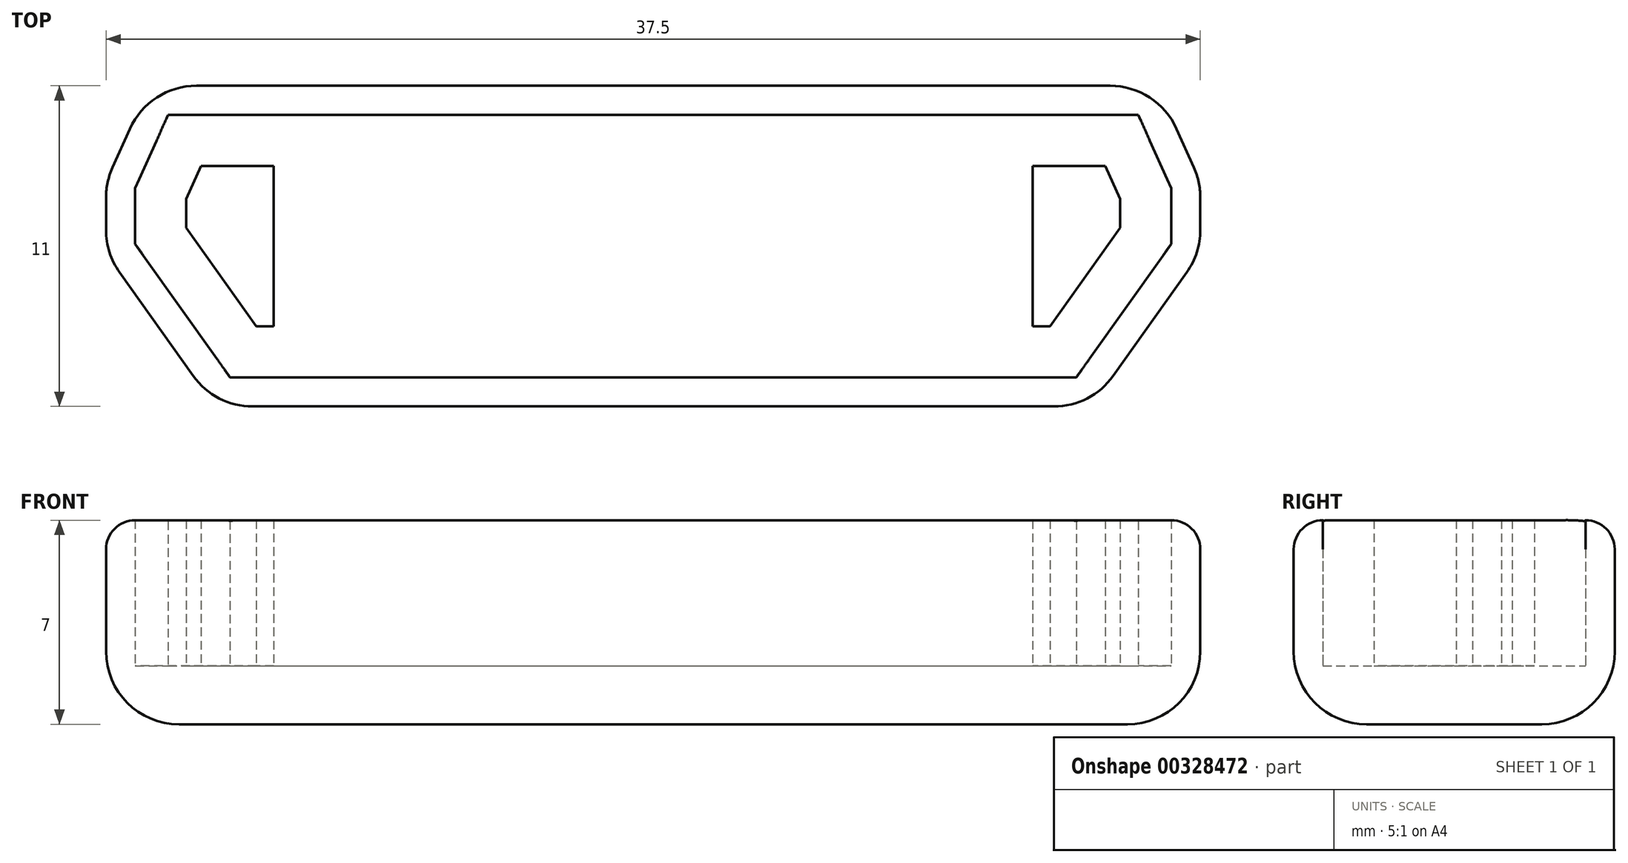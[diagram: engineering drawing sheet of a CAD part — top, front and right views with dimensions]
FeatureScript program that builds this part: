
annotation { "Feature Type Name" : "Feature", "Feature Type Description" : "" }
export const myFeature = defineFeature(function(context is Context, id is Id, definition is map)
    precondition{}
    {
        {
            var Q0;
            Q0=qCreatedBy(makeId("Top.planeOp"),FACE);
            var sketch = newSketch(context, id + "F0", { "sketchPlane" : qUnion([Q0])});
            skLineSegment(sketch, "E0", {"start": v(0, 0) * mm, "end": v(0, 26.86) * mm, "construction": true});
            skLineSegment(sketch, "E1", {"start": v(0, 0) * mm, "end": v(14.5, 0) * mm});
            skLineSegment(sketch, "E2", {"start": v(14.5, 0) * mm, "end": v(17.75, 4.57) * mm});
            skLineSegment(sketch, "E3", {"start": v(17.75, 4.57) * mm, "end": v(17.75, 6.5) * mm});
            skLineSegment(sketch, "E4", {"start": v(17.75, 6.5) * mm, "end": v(16.62, 9) * mm});
            skLineSegment(sketch, "E5", {"start": v(16.62, 9) * mm, "end": v(0, 9) * mm});
            skLineSegment(sketch, "E6.0", {"start": v(17.27, 10) * mm, "end": v(0, 10) * mm});
            skLineSegment(sketch, "E6.1", {"start": v(0, -1) * mm, "end": v(15.02, -1) * mm});
            skLineSegment(sketch, "E6.2", {"start": v(15.02, -1) * mm, "end": v(18.75, 4.25) * mm});
            skLineSegment(sketch, "E6.3", {"start": v(18.75, 4.25) * mm, "end": v(18.75, 6.7) * mm});
            skLineSegment(sketch, "E6.4", {"start": v(18.75, 6.7) * mm, "end": v(17.27, 10) * mm});
            skLineSegment(sketch, "E7.0", {"start": v(15.5, 7.25) * mm, "end": v(13, 7.25) * mm});
            skLineSegment(sketch, "E7.1", {"start": v(13, 1.75) * mm, "end": v(13.6, 1.75) * mm});
            skLineSegment(sketch, "E7.2", {"start": v(13.6, 1.75) * mm, "end": v(16, 5.13) * mm});
            skLineSegment(sketch, "E7.3", {"start": v(16, 5.13) * mm, "end": v(16, 6.12) * mm});
            skLineSegment(sketch, "E7.4", {"start": v(16, 6.12) * mm, "end": v(15.5, 7.25) * mm});
            skLineSegment(sketch, "E8", {"start": v(13, 7.25) * mm, "end": v(13, 1.75) * mm});
            skLineSegment(sketch, "E9.MirrorCS", {"start": v(-16, 6.12) * mm, "end": v(-15.5, 7.25) * mm});
            skLineSegment(sketch, "E10.MirrorCS", {"start": v(-16, 5.13) * mm, "end": v(-16, 6.12) * mm});
            skLineSegment(sketch, "E11.MirrorCS", {"start": v(-13, 1.75) * mm, "end": v(-13.6, 1.75) * mm});
            skLineSegment(sketch, "E12.MirrorCS", {"start": v(-18.75, 4.25) * mm, "end": v(-18.75, 6.7) * mm});
            skLineSegment(sketch, "E13.MirrorCS", {"start": v(-17.75, 4.57) * mm, "end": v(-17.75, 6.5) * mm});
            skLineSegment(sketch, "E14.MirrorCS", {"start": v(-13, 7.25) * mm, "end": v(-13, 1.75) * mm});
            skLineSegment(sketch, "E15.MirrorCS", {"start": v(-13.6, 1.75) * mm, "end": v(-16, 5.13) * mm});
            skLineSegment(sketch, "E16.MirrorCS", {"start": v(-15.5, 7.25) * mm, "end": v(-13, 7.25) * mm});
            skLineSegment(sketch, "E17.MirrorCS", {"start": v(-18.75, 6.7) * mm, "end": v(-17.27, 10) * mm});
            skLineSegment(sketch, "E18.MirrorCS", {"start": v(-15.02, -1) * mm, "end": v(-18.75, 4.25) * mm});
            skLineSegment(sketch, "E19.MirrorCS", {"start": v(0, -1) * mm, "end": v(-15.02, -1) * mm});
            skLineSegment(sketch, "E20.MirrorCS", {"start": v(-17.27, 10) * mm, "end": v(0, 10) * mm});
            skLineSegment(sketch, "E21.MirrorCS", {"start": v(-16.62, 9) * mm, "end": v(0, 9) * mm});
            skLineSegment(sketch, "E22.MirrorCS", {"start": v(0, 0) * mm, "end": v(-14.5, 0) * mm});
            skLineSegment(sketch, "E23.MirrorCS", {"start": v(-17.75, 6.5) * mm, "end": v(-16.62, 9) * mm});
            skLineSegment(sketch, "E24.MirrorCS", {"start": v(-14.5, 0) * mm, "end": v(-17.75, 4.57) * mm});
            skSolve(sketch);
        }
        {
            var Q0;
            Q0=makeQuery(id+"F0.imprint","IMPRINT",FACE,{"disambiguationData":[TD([[makeQuery(id+"F0.imprint","IMPRINT",EDGE,{"derivedFrom":sQuery(id+"F0.wireOp",EDGE,"E1")}),-1.0]])]});
            var Q1;
            Q1=makeQuery(id+"F0.imprint","IMPRINT",FACE,{"disambiguationData":[TD([[makeQuery(id+"F0.imprint","IMPRINT",EDGE,{"derivedFrom":sQuery(id+"F0.wireOp",EDGE,"E9.MirrorCS")}),-1.0]])]});
            var Q2;
            Q2=makeQuery(id+"F0.imprint","IMPRINT",FACE,{"disambiguationData":[TD([[makeQuery(id+"F0.imprint","IMPRINT",EDGE,{"derivedFrom":sQuery(id+"F0.wireOp",EDGE,"E7.0")}),1.0]])]});
            extrude(context, id + "F1", {"entities" : qUnion([Q0, Q1, Q2]), "depth" : 5 * mm});
        }
        {
            var Q0;
            Q0=makeQuery(id+"F1.opExtrude","CAP_FACE",FACE,{"disambiguationData":[OSD([sQuery(id+"F0.wireOp",EDGE,"E1"),sQuery(id+"F0.wireOp",EDGE,"E2"),sQuery(id+"F0.wireOp",EDGE,"E3"),sQuery(id+"F0.wireOp",EDGE,"E4"),sQuery(id+"F0.wireOp",EDGE,"E5"),sQuery(id+"F0.wireOp",EDGE,"E6.0"),sQuery(id+"F0.wireOp",EDGE,"E6.1"),sQuery(id+"F0.wireOp",EDGE,"E6.2"),sQuery(id+"F0.wireOp",EDGE,"E6.3"),sQuery(id+"F0.wireOp",EDGE,"E6.4"),sQuery(id+"F0.wireOp",EDGE,"E12.MirrorCS"),sQuery(id+"F0.wireOp",EDGE,"E13.MirrorCS"),sQuery(id+"F0.wireOp",EDGE,"E17.MirrorCS"),sQuery(id+"F0.wireOp",EDGE,"E18.MirrorCS"),sQuery(id+"F0.wireOp",EDGE,"E19.MirrorCS"),sQuery(id+"F0.wireOp",EDGE,"E20.MirrorCS"),sQuery(id+"F0.wireOp",EDGE,"E21.MirrorCS"),sQuery(id+"F0.wireOp",EDGE,"E22.MirrorCS"),sQuery(id+"F0.wireOp",EDGE,"E23.MirrorCS"),sQuery(id+"F0.wireOp",EDGE,"E24.MirrorCS")])],"isStart":true});
            var sketch = newSketch(context, id + "F2", { "sketchPlane" : qUnion([Q0])});
            skLineSegment(sketch, "E25.0", {"start": v(17.27, -10) * mm, "end": v(-17.27, -10) * mm});
            skLineSegment(sketch, "E25.1", {"start": v(-18.75, -6.7) * mm, "end": v(-17.27, -10) * mm});
            skLineSegment(sketch, "E25.2", {"start": v(-18.75, -4.25) * mm, "end": v(-18.75, -6.7) * mm});
            skLineSegment(sketch, "E25.3", {"start": v(-15.02, 1) * mm, "end": v(-18.75, -4.25) * mm});
            skLineSegment(sketch, "E25.4", {"start": v(15.02, 1) * mm, "end": v(-15.02, 1) * mm});
            skLineSegment(sketch, "E25.5", {"start": v(15.02, 1) * mm, "end": v(18.75, -4.25) * mm});
            skLineSegment(sketch, "E25.6", {"start": v(18.75, -4.25) * mm, "end": v(18.75, -6.7) * mm});
            skLineSegment(sketch, "E25.7", {"start": v(18.75, -6.7) * mm, "end": v(17.27, -10) * mm});
            skSolve(sketch);
        }
        {
            var Q0;
            Q0 = qSketchRegion(id + "F2", true);
            extrude(context, id + "F3", {"entities" : qUnion([Q0]), "operationType" : NewBodyOperationType.ADD, "depth" : 2 * mm});
        }
        {
            var Q0;
            Q0=makeQuery(id+"F3.opExtrude","CAP_FACE",FACE,{"disambiguationData":[OSD([sQuery(id+"F2.wireOp",EDGE,"E25.0"),sQuery(id+"F2.wireOp",EDGE,"E25.1"),sQuery(id+"F2.wireOp",EDGE,"E25.2"),sQuery(id+"F2.wireOp",EDGE,"E25.3"),sQuery(id+"F2.wireOp",EDGE,"E25.4"),sQuery(id+"F2.wireOp",EDGE,"E25.5"),sQuery(id+"F2.wireOp",EDGE,"E25.6"),sQuery(id+"F2.wireOp",EDGE,"E25.7")])],"isStart":false});
            var Q1;
            Q1=makeQuery(id+"F3.boolean.opBoolean","MERGE",EDGE,{"derivedFrom":[makeQuery(id+"F1.opExtrude","SWEPT_EDGE",EDGE,{"disambiguationData":[OSD([sQuery(id+"F0.wireOp",EDGE,"E18.MirrorCS"),sQuery(id+"F0.wireOp",EDGE,"E19.MirrorCS")])]}),makeQuery(id+"F3.opExtrude","SWEPT_EDGE",EDGE,{"disambiguationData":[OSD([sQuery(id+"F2.wireOp",EDGE,"E25.3"),sQuery(id+"F2.wireOp",EDGE,"E25.4")])]})]});
            var Q2;
            Q2=makeQuery(id+"F3.boolean.opBoolean","MERGE",EDGE,{"derivedFrom":[makeQuery(id+"F1.opExtrude","SWEPT_EDGE",EDGE,{"disambiguationData":[OSD([sQuery(id+"F0.wireOp",EDGE,"E12.MirrorCS"),sQuery(id+"F0.wireOp",EDGE,"E18.MirrorCS")])]}),makeQuery(id+"F3.opExtrude","SWEPT_EDGE",EDGE,{"disambiguationData":[OSD([sQuery(id+"F2.wireOp",EDGE,"E25.2"),sQuery(id+"F2.wireOp",EDGE,"E25.3")])]})]});
            var Q3;
            Q3=makeQuery(id+"F3.boolean.opBoolean","MERGE",EDGE,{"derivedFrom":[makeQuery(id+"F1.opExtrude","SWEPT_EDGE",EDGE,{"disambiguationData":[OSD([sQuery(id+"F0.wireOp",EDGE,"E12.MirrorCS"),sQuery(id+"F0.wireOp",EDGE,"E17.MirrorCS")])]}),makeQuery(id+"F3.opExtrude","SWEPT_EDGE",EDGE,{"disambiguationData":[OSD([sQuery(id+"F2.wireOp",EDGE,"E25.1"),sQuery(id+"F2.wireOp",EDGE,"E25.2")])]})]});
            var Q4;
            Q4=makeQuery(id+"F3.boolean.opBoolean","MERGE",EDGE,{"derivedFrom":[makeQuery(id+"F1.opExtrude","SWEPT_EDGE",EDGE,{"disambiguationData":[OSD([sQuery(id+"F0.wireOp",EDGE,"E17.MirrorCS"),sQuery(id+"F0.wireOp",EDGE,"E20.MirrorCS")])]}),makeQuery(id+"F3.opExtrude","SWEPT_EDGE",EDGE,{"disambiguationData":[OSD([sQuery(id+"F2.wireOp",EDGE,"E25.0"),sQuery(id+"F2.wireOp",EDGE,"E25.1")])]})]});
            var Q5;
            Q5=makeQuery(id+"F3.boolean.opBoolean","MERGE",EDGE,{"derivedFrom":[makeQuery(id+"F1.opExtrude","SWEPT_EDGE",EDGE,{"disambiguationData":[OSD([sQuery(id+"F0.wireOp",EDGE,"E6.1"),sQuery(id+"F0.wireOp",EDGE,"E6.2")])]}),makeQuery(id+"F3.opExtrude","SWEPT_EDGE",EDGE,{"disambiguationData":[OSD([sQuery(id+"F2.wireOp",EDGE,"E25.4"),sQuery(id+"F2.wireOp",EDGE,"E25.5")])]})]});
            var Q6;
            Q6=makeQuery(id+"F3.boolean.opBoolean","MERGE",EDGE,{"derivedFrom":[makeQuery(id+"F1.opExtrude","SWEPT_EDGE",EDGE,{"disambiguationData":[OSD([sQuery(id+"F0.wireOp",EDGE,"E6.2"),sQuery(id+"F0.wireOp",EDGE,"E6.3")])]}),makeQuery(id+"F3.opExtrude","SWEPT_EDGE",EDGE,{"disambiguationData":[OSD([sQuery(id+"F2.wireOp",EDGE,"E25.5"),sQuery(id+"F2.wireOp",EDGE,"E25.6")])]})]});
            var Q7;
            Q7=makeQuery(id+"F3.boolean.opBoolean","MERGE",EDGE,{"derivedFrom":[makeQuery(id+"F1.opExtrude","SWEPT_EDGE",EDGE,{"disambiguationData":[OSD([sQuery(id+"F0.wireOp",EDGE,"E6.0"),sQuery(id+"F0.wireOp",EDGE,"E6.4")])]}),makeQuery(id+"F3.opExtrude","SWEPT_EDGE",EDGE,{"disambiguationData":[OSD([sQuery(id+"F2.wireOp",EDGE,"E25.0"),sQuery(id+"F2.wireOp",EDGE,"E25.7")])]})]});
            var Q8;
            Q8=makeQuery(id+"F3.boolean.opBoolean","MERGE",EDGE,{"derivedFrom":[makeQuery(id+"F1.opExtrude","SWEPT_EDGE",EDGE,{"disambiguationData":[OSD([sQuery(id+"F0.wireOp",EDGE,"E6.3"),sQuery(id+"F0.wireOp",EDGE,"E6.4")])]}),makeQuery(id+"F3.opExtrude","SWEPT_EDGE",EDGE,{"disambiguationData":[OSD([sQuery(id+"F2.wireOp",EDGE,"E25.6"),sQuery(id+"F2.wireOp",EDGE,"E25.7")])]})]});
            fillet(context, id + "F4", {"entities" : qUnion([Q0, Q1, Q2, Q3, Q4, Q5, Q6, Q7, Q8]), "radius" : 2.5 * mm, "tangentPropagation" : true, "allowEdgeOverflow" : false});
        }
        {
            var Q0;
            Q0=makeQuery(id+"F1.opExtrude","CAP_EDGE",EDGE,{"disambiguationData":[OSD([sQuery(id+"F0.wireOp",EDGE,"E6.1"),sQuery(id+"F0.wireOp",EDGE,"E19.MirrorCS")])],"isStart":false});
            fillet(context, id + "F5", {"entities" : qUnion([Q0]), "radius" : 1 * mm, "tangentPropagation" : true, "allowEdgeOverflow" : false});
        }
    });
